# Revit family: Trane_TVR_Indoor_Wall mounted_4TVW0012(15)EF000AA(2nd DC)
name_source: partatom
category: Equipamento mecânico
units: mm (PartAtom-declared; Revit-internal decimal feet)

## family parameters
Com base no plano de trabalho = Não
Compartilhado = Não
Corte com vazios quando carregada = Não
Cota do conector redondo = Utilizar diâmetro
Número OmniClass = 23.75.00.00
Ponto de cálculo do ambiente = Não
Sempre na vertical = Sim
Tipo de parte = Normal
Título OmniClass = Climate Control (HVAC)

## types (2) — shared parameters
Condensation = air
Depth = 223  [stored 0.731627 ft]
Descrição = High efficiency air cooled
Fabricante = Trane
Gas = R410a
Gas pipe = 12.7  [stored 0.0416667 ft]
Height = 315  [stored 1.03346 ft]
Installation = Indoor installation
Liquid pipe = 6.35  [stored 0.0208333 ft]
Machine material = Galvanized Steel
Maximum Fuse Amps = 15 A
Minimum Circuit Amps = 0 A
Panel color = S1022
Power supply = 220-240V ~50/60Hz
Series = TVR ULTRA
URL = https://www.trane.com
Width = 990  [stored 3.24803 ft]
zero-valued in all types: clearance access behind, clearance access front, clearance access left, clearance access right

## per-type parameters (varying)
| type | Air  Flow | Cooling Capacity | Cooling Power Input | Heating Capacity | Heating Power Input | Net Weight |
| 4TVW0012EF000AA | 656/628/591/573/544/515/488 m3/h | 4 kW | 30 W | 4 kW | 30 W | 11.40 kg |
| 4TVW0015EF000AA | 594/563/535/507/478/450/424 m3/h | 5 kW | 40 W | 5 kW | 40 W | 12.80 kg |

note: column(s) folded — value = type name in every type: Modelo

note: [stored X ft] marks values corroborated as IEEE doubles in the binary element streams (Revit-internal decimal feet)
